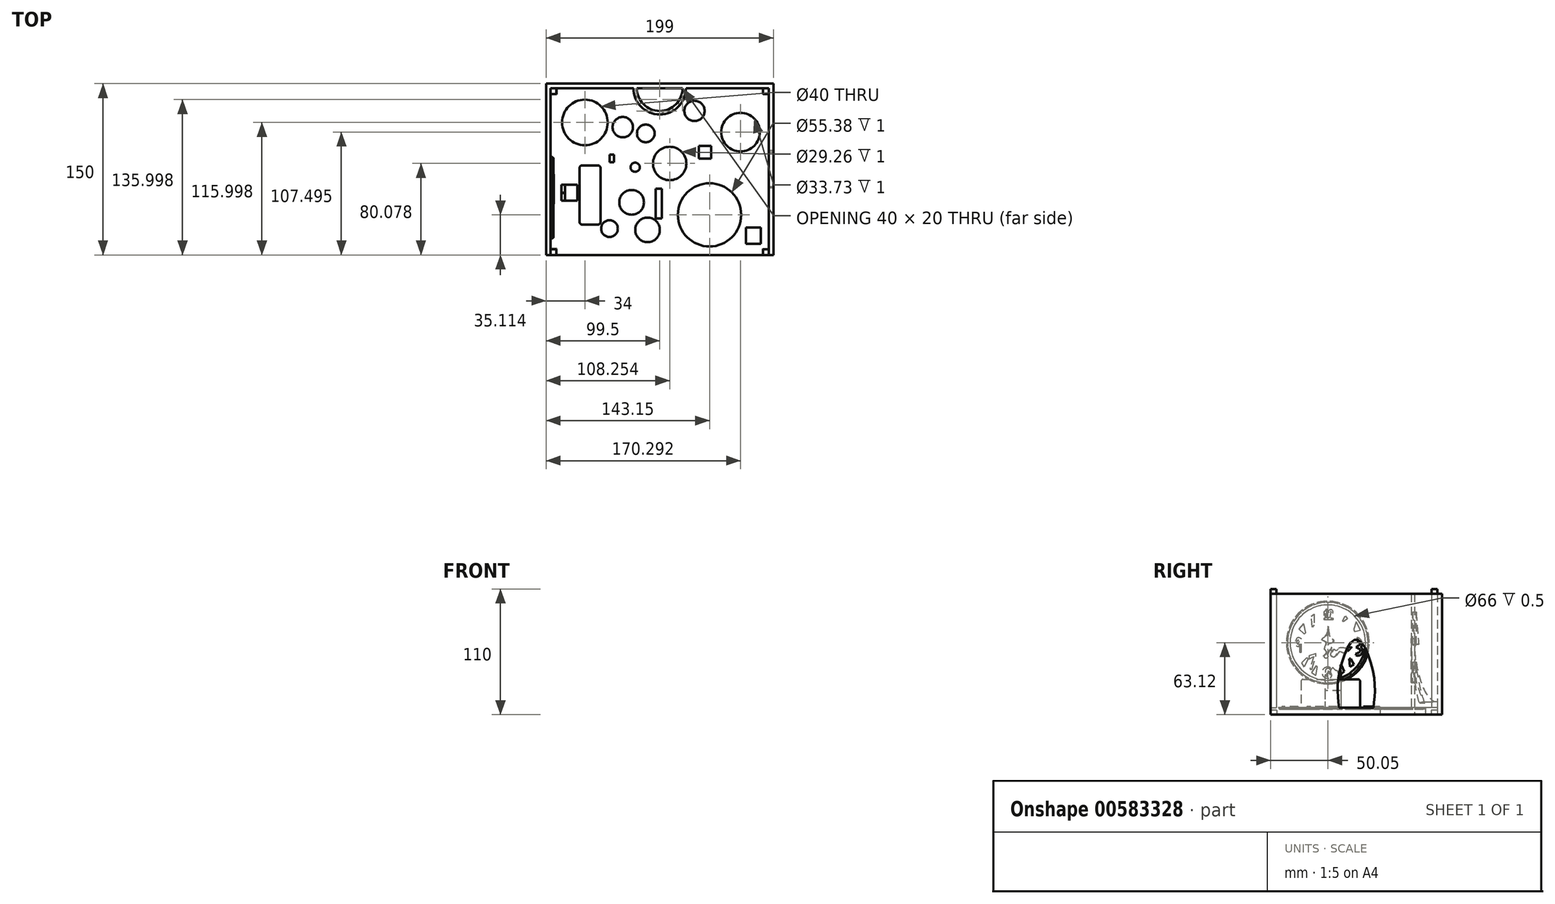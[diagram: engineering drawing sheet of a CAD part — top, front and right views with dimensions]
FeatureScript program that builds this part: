
annotation { "Feature Type Name" : "Feature", "Feature Type Description" : "" }
export const myFeature = defineFeature(function(context is Context, id is Id, definition is map)
    precondition{}
    {
        {
            var Q0;
            Q0=qCreatedBy(makeId("Top.planeOp"),FACE);
            var sketch = newSketch(context, id + "F0", { "sketchPlane" : qUnion([Q0])});
            skLineSegment(sketch, "E0.bottom", {"start": v(-124.6, 78.2) * mm, "end": v(74.4, 78.2) * mm});
            skLineSegment(sketch, "E0.top", {"start": v(-124.6, -71.8) * mm, "end": v(74.4, -71.8) * mm});
            skLineSegment(sketch, "E0.left", {"start": v(-124.6, 78.2) * mm, "end": v(-124.6, -71.8) * mm});
            skLineSegment(sketch, "E0.right", {"start": v(74.4, 78.2) * mm, "end": v(74.4, -71.8) * mm});
            skLineSegment(sketch, "E1.0", {"start": v(-120.6, 74.2) * mm, "end": v(-120.6, -71.8) * mm});
            skLineSegment(sketch, "E1.1", {"start": v(-120.6, 74.2) * mm, "end": v(70.4, 74.2) * mm});
            skLineSegment(sketch, "E1.2", {"start": v(70.4, 74.2) * mm, "end": v(70.4, -71.8) * mm});
            skSolve(sketch);
        }
        {
            var Q0;
            Q0 = qSketchRegion(id + "F0", true);
            extrude(context, id + "F1", {"entities" : qUnion([Q0]), "depth" : 6 * mm, "offsetDistance" : 25 * mm});
        }
        {
            var Q0;
            Q0=makeQuery(id+"F1.opExtrude","CAP_FACE",FACE,{"disambiguationData":[OSD([sQuery(id+"F0.wireOp",EDGE,"E0.bottom"),sQuery(id+"F0.wireOp",EDGE,"E0.top"),sQuery(id+"F0.wireOp",EDGE,"E0.left"),sQuery(id+"F0.wireOp",EDGE,"E0.right")])],"isStart":false});
            var sketch = newSketch(context, id + "F2", { "sketchPlane" : qUnion([Q0])});
            skLineSegment(sketch, "E2.0", {"start": v(-120.6, 74.2) * mm, "end": v(-120.6, -71.8) * mm});
            skLineSegment(sketch, "E2.1", {"start": v(-120.6, 74.2) * mm, "end": v(70.4, 74.2) * mm});
            skLineSegment(sketch, "E2.2", {"start": v(70.4, 74.2) * mm, "end": v(70.4, -71.8) * mm});
            skLineSegment(sketch, "E3", {"start": v(-120.6, -71.8) * mm, "end": v(-124.6, -71.8) * mm});
            skLineSegment(sketch, "E4", {"start": v(-124.6, -71.8) * mm, "end": v(-124.6, 78.2) * mm});
            skLineSegment(sketch, "E5", {"start": v(-124.6, 78.2) * mm, "end": v(74.4, 78.2) * mm});
            skLineSegment(sketch, "E6", {"start": v(74.4, 78.2) * mm, "end": v(74.4, -71.8) * mm});
            skLineSegment(sketch, "E7", {"start": v(74.4, -71.8) * mm, "end": v(70.4, -71.8) * mm});
            skPoint(sketch, "E8.start.orphan", {"position": v(-25.1, 64.2) * mm});
            skArc(sketch, "E9", {"start": v(-45.1, 74.2) * mm, "mid": v(-25.1, 54.2) * mm, "end": v(-5.1, 74.2) * mm});
            skArc(sketch, "E10.0", {"start": v(-48.1, 74.2) * mm, "mid": v(-25.1, 51.2) * mm, "end": v(-2.1, 74.2) * mm});
            skSolve(sketch);
        }
        {
            var Q0;
            Q0 = qSketchRegion(id + "F2", true);
            extrude(context, id + "F3", {"entities" : qUnion([Q0]), "operationType" : NewBodyOperationType.ADD, "depth" : 100 * mm, "offsetDistance" : 25 * mm});
        }
        {
            var Q0;
            Q0=makeQuery(id+"F3.boolean.opBoolean","MERGE",FACE,{"derivedFrom":[makeQuery(id+"F1.opExtrude","SWEPT_FACE",FACE,{"disambiguationData":[OSD([sQuery(id+"F0.wireOp",EDGE,"E0.right")])]}),makeQuery(id+"F3.opExtrude","SWEPT_FACE",FACE,{"disambiguationData":[OSD([sQuery(id+"F2.wireOp",EDGE,"E6")])]})]});
            var sketch = newSketch(context, id + "F4", { "sketchPlane" : qUnion([Q0])});
            skLineSegment(sketch, "E11", {"start": v(3.2, 6) * mm, "end": v(-11.8, 6) * mm});
            skLineSegment(sketch, "E12", {"start": v(3.2, 6) * mm, "end": v(18.2, 6) * mm});
            skPoint(sketch, "E13.start.orphan", {"position": v(3.2, 0) * mm});
            skPoint(sketch, "E14.1.internal.snap0", {"position": v(3.2, 36) * mm});
            skPoint(sketch, "E14.3.internal.snap0", {"position": v(3.2, 36) * mm});
            skFitSpline(sketch, "E14", {"points": [v(-11.8, 6) * mm, v(-11.8, 36) * mm, v(3.2, 66) * mm, v(18.2, 36) * mm, v(18.2, 6) * mm], "startDerivative": vector(-14.19, 109.03) * mm, "endDerivative": vector(-14.19, -109.03) * mm});
            skSolve(sketch);
        }
        {
            var Q0;
            Q0 = qSketchRegion(id + "F4", true);
            extrude(context, id + "F5", {"entities" : qUnion([Q0]), "operationType" : NewBodyOperationType.REMOVE, "oppositeDirection" : true, "depth" : 4 * mm, "offsetDistance" : 25 * mm});
        }
        {
            var Q0;
            Q0=makeQuery(id+"F1.opExtrude","CAP_FACE",FACE,{"disambiguationData":[OSD([sQuery(id+"F0.wireOp",EDGE,"E0.bottom"),sQuery(id+"F0.wireOp",EDGE,"E0.top"),sQuery(id+"F0.wireOp",EDGE,"E0.left"),sQuery(id+"F0.wireOp",EDGE,"E0.right")])],"isStart":true});
            var sketch = newSketch(context, id + "F6", { "sketchPlane" : qUnion([Q0])});
            skLineSegment(sketch, "E15.0", {"start": v(-120.6, -74.2) * mm, "end": v(-120.6, 71.8) * mm});
            skLineSegment(sketch, "E15.1", {"start": v(-120.6, -74.2) * mm, "end": v(70.4, -74.2) * mm});
            skLineSegment(sketch, "E15.2", {"start": v(70.4, -74.2) * mm, "end": v(70.4, 71.8) * mm});
            skLineSegment(sketch, "E16.bottom", {"start": v(-120.6, -74.2) * mm, "end": v(-115.1, -74.2) * mm});
            skLineSegment(sketch, "E16.top", {"start": v(-120.6, -68.7) * mm, "end": v(-115.1, -68.7) * mm});
            skLineSegment(sketch, "E16.left", {"start": v(-120.6, -74.2) * mm, "end": v(-120.6, -68.7) * mm});
            skLineSegment(sketch, "E16.right", {"start": v(-115.1, -74.2) * mm, "end": v(-115.1, -68.7) * mm});
            skLineSegment(sketch, "E17", {"start": v(70.4, 71.8) * mm, "end": v(64.9, 71.8) * mm});
            skLineSegment(sketch, "E18", {"start": v(64.9, 71.8) * mm, "end": v(64.9, 66.3) * mm});
            skLineSegment(sketch, "E19", {"start": v(64.9, 66.3) * mm, "end": v(70.4, 66.3) * mm});
            skLineSegment(sketch, "E20", {"start": v(70.4, 66.3) * mm, "end": v(70.4, 71.8) * mm});
            skLineSegment(sketch, "E21", {"start": v(-120.6, 71.8) * mm, "end": v(-115.1, 71.8) * mm});
            skLineSegment(sketch, "E22", {"start": v(-115.1, 71.8) * mm, "end": v(-115.1, 66.3) * mm});
            skLineSegment(sketch, "E23", {"start": v(-115.1, 66.3) * mm, "end": v(-120.6, 66.3) * mm});
            skLineSegment(sketch, "E24", {"start": v(-120.6, 66.3) * mm, "end": v(-120.6, 71.8) * mm});
            skLineSegment(sketch, "E25.bottom", {"start": v(70.4, -74.2) * mm, "end": v(64.9, -74.2) * mm});
            skLineSegment(sketch, "E25.top", {"start": v(70.4, -68.7) * mm, "end": v(64.9, -68.7) * mm});
            skLineSegment(sketch, "E25.left", {"start": v(70.4, -74.2) * mm, "end": v(70.4, -68.7) * mm});
            skLineSegment(sketch, "E25.right", {"start": v(64.9, -74.2) * mm, "end": v(64.9, -68.7) * mm});
            skSolve(sketch);
        }
        {
            var Q0;
            Q0 = qSketchRegion(id + "F6", true);
            extrude(context, id + "F7", {"entities" : qUnion([Q0]), "operationType" : NewBodyOperationType.REMOVE, "oppositeDirection" : true, "depth" : 4 * mm, "offsetDistance" : 25 * mm});
        }
        {
            var Q0;
            {var subQ4=sQuery(id+"F0.wireOp",EDGE,"E0.top");Q0=makeQuery(id+"F5.boolean.opBoolean","MERGE",FACE,{"derivedFrom":[makeQuery(id+"F3.boolean.opBoolean","SPLIT",FACE,{"disambiguationData":[TD([makeQuery(id+"F1.opExtrude","SWEPT_FACE",FACE,{"disambiguationData":[OSD([subQ4])]})])],"derivedFrom":makeQuery(id+"F1.opExtrude","CAP_FACE",FACE,{"disambiguationData":[OSD([sQuery(id+"F0.wireOp",EDGE,"E0.bottom"),subQ4,sQuery(id+"F0.wireOp",EDGE,"E0.left"),sQuery(id+"F0.wireOp",EDGE,"E0.right")])],"isStart":false})}),makeQuery(id+"F5.opExtrude","SWEPT_FACE",FACE,{"disambiguationData":[OSD([sQuery(id+"F4.wireOp",EDGE,"E11"),sQuery(id+"F4.wireOp",EDGE,"E12")])]})]});}
            var sketch = newSketch(context, id + "F8", { "sketchPlane" : qUnion([Q0])});
            skLineSegment(sketch, "E26.bottom", {"start": v(-120.6, 74.2) * mm, "end": v(-115.6, 74.2) * mm});
            skLineSegment(sketch, "E26.top", {"start": v(-120.6, 69.2) * mm, "end": v(-115.6, 69.2) * mm});
            skLineSegment(sketch, "E26.left", {"start": v(-120.6, 74.2) * mm, "end": v(-120.6, 69.2) * mm});
            skLineSegment(sketch, "E26.right", {"start": v(-115.6, 74.2) * mm, "end": v(-115.6, 69.2) * mm});
            skLineSegment(sketch, "E27.bottom", {"start": v(-120.6, -71.8) * mm, "end": v(-115.6, -71.8) * mm});
            skLineSegment(sketch, "E27.top", {"start": v(-120.6, -66.8) * mm, "end": v(-115.6, -66.8) * mm});
            skLineSegment(sketch, "E27.left", {"start": v(-120.6, -71.8) * mm, "end": v(-120.6, -66.8) * mm});
            skLineSegment(sketch, "E27.right", {"start": v(-115.6, -71.8) * mm, "end": v(-115.6, -66.8) * mm});
            skLineSegment(sketch, "E28.bottom", {"start": v(70.4, -71.8) * mm, "end": v(65.4, -71.8) * mm});
            skLineSegment(sketch, "E28.top", {"start": v(70.4, -66.8) * mm, "end": v(65.4, -66.8) * mm});
            skLineSegment(sketch, "E28.left", {"start": v(70.4, -71.8) * mm, "end": v(70.4, -66.8) * mm});
            skLineSegment(sketch, "E28.right", {"start": v(65.4, -71.8) * mm, "end": v(65.4, -66.8) * mm});
            skLineSegment(sketch, "E29.bottom", {"start": v(70.4, 74.2) * mm, "end": v(65.4, 74.2) * mm});
            skLineSegment(sketch, "E29.top", {"start": v(70.4, 69.2) * mm, "end": v(65.4, 69.2) * mm});
            skLineSegment(sketch, "E29.left", {"start": v(70.4, 74.2) * mm, "end": v(70.4, 69.2) * mm});
            skLineSegment(sketch, "E29.right", {"start": v(65.4, 74.2) * mm, "end": v(65.4, 69.2) * mm});
            skSolve(sketch);
        }
        {
            var Q0;
            Q0 = qSketchRegion(id + "F8", true);
            extrude(context, id + "F9", {"entities" : qUnion([Q0]), "operationType" : NewBodyOperationType.ADD, "depth" : 104 * mm, "offsetDistance" : 25 * mm});
        }
        {
            var Q0;
            {var subQ4=sQuery(id+"F0.wireOp",EDGE,"E0.top");Q0=makeQuery(id+"F5.boolean.opBoolean","MERGE",FACE,{"derivedFrom":[makeQuery(id+"F3.boolean.opBoolean","SPLIT",FACE,{"disambiguationData":[TD([makeQuery(id+"F1.opExtrude","SWEPT_FACE",FACE,{"disambiguationData":[OSD([subQ4])]})])],"derivedFrom":makeQuery(id+"F1.opExtrude","CAP_FACE",FACE,{"disambiguationData":[OSD([sQuery(id+"F0.wireOp",EDGE,"E0.bottom"),subQ4,sQuery(id+"F0.wireOp",EDGE,"E0.left"),sQuery(id+"F0.wireOp",EDGE,"E0.right")])],"isStart":false})}),makeQuery(id+"F5.opExtrude","SWEPT_FACE",FACE,{"disambiguationData":[OSD([sQuery(id+"F4.wireOp",EDGE,"E11"),sQuery(id+"F4.wireOp",EDGE,"E12")])]})]});}
            var sketch = newSketch(context, id + "F10", { "sketchPlane" : qUnion([Q0])});
            skCircle(sketch, "E30", {"center": v(-90.6, 44.2) * mm, "radius": 20 * mm});
            skSolve(sketch);
        }
        {
            var Q0;
            Q0 = qSketchRegion(id + "F10", true);
            extrude(context, id + "F11", {"entities" : qUnion([Q0]), "operationType" : NewBodyOperationType.REMOVE, "oppositeDirection" : true, "depth" : 25 * mm, "offsetDistance" : 25 * mm});
        }
        {
            var Q0;
            {var subQ0=sQuery(id+"F2.wireOp",EDGE,"E9");Q0=makeQuery(id+"F3.boolean.opBoolean","SPLIT",FACE,{"disambiguationData":[TD([makeQuery(id+"F3.opExtrude","SWEPT_FACE",FACE,{"disambiguationData":[OSD([subQ0])]})])],"derivedFrom":makeQuery(id+"F1.opExtrude","CAP_FACE",FACE,{"disambiguationData":[OSD([sQuery(id+"F0.wireOp",EDGE,"E0.bottom"),sQuery(id+"F0.wireOp",EDGE,"E0.top"),sQuery(id+"F0.wireOp",EDGE,"E0.left"),sQuery(id+"F0.wireOp",EDGE,"E0.right")])],"isStart":false})});}
            var sketch = newSketch(context, id + "F12", { "sketchPlane" : qUnion([Q0])});
            skSolve(sketch);
        }
        {
            var Q0;
            {var subQ0=sQuery(id+"F2.wireOp",EDGE,"E9");Q0=makeQuery(id+"F12.imprint","IMPRINT",FACE,{"disambiguationData":[TD([[makeQuery(id+"F12.imprint","IMPRINT",EDGE,{"derivedFrom":makeQuery(id+"F3.opExtrude","CAP_EDGE",EDGE,{"disambiguationData":[OSD([subQ0])],"isStart":true})}),1.0]])]});}
            extrude(context, id + "F13", {"entities" : qUnion([Q0]), "operationType" : NewBodyOperationType.REMOVE, "oppositeDirection" : true, "depth" : 25 * mm, "offsetDistance" : 25 * mm});
        }
        {
            var Q0;
            {var subQ4=sQuery(id+"F0.wireOp",EDGE,"E0.top");Q0=makeQuery(id+"F5.boolean.opBoolean","MERGE",FACE,{"derivedFrom":[makeQuery(id+"F3.boolean.opBoolean","SPLIT",FACE,{"disambiguationData":[TD([makeQuery(id+"F1.opExtrude","SWEPT_FACE",FACE,{"disambiguationData":[OSD([subQ4])]})])],"derivedFrom":makeQuery(id+"F1.opExtrude","CAP_FACE",FACE,{"disambiguationData":[OSD([sQuery(id+"F0.wireOp",EDGE,"E0.bottom"),subQ4,sQuery(id+"F0.wireOp",EDGE,"E0.left"),sQuery(id+"F0.wireOp",EDGE,"E0.right")])],"isStart":false})}),makeQuery(id+"F5.opExtrude","SWEPT_FACE",FACE,{"disambiguationData":[OSD([sQuery(id+"F4.wireOp",EDGE,"E11"),sQuery(id+"F4.wireOp",EDGE,"E12")])]})]});}
            var sketch = newSketch(context, id + "F14", { "sketchPlane" : qUnion([Q0])});
            skLineSegment(sketch, "E31.bottom", {"start": v(-95.22, -45.16) * mm, "end": v(-77.03, -45.16) * mm});
            skLineSegment(sketch, "E31.top", {"start": v(-95.22, 6.58) * mm, "end": v(-77.03, 6.58) * mm});
            skLineSegment(sketch, "E31.left", {"start": v(-95.22, -45.16) * mm, "end": v(-95.22, 6.58) * mm});
            skLineSegment(sketch, "E31.right", {"start": v(-77.03, -45.16) * mm, "end": v(-77.03, 6.58) * mm});
            skSolve(sketch);
        }
        {
            var Q0;
            Q0 = qSketchRegion(id + "F14", true);
            extrude(context, id + "F15", {"entities" : qUnion([Q0]), "operationType" : NewBodyOperationType.ADD, "depth" : 25 * mm, "offsetDistance" : 25 * mm});
        }
        {
            var Q0;
            {var subQ4=sQuery(id+"F0.wireOp",EDGE,"E0.top");Q0=makeQuery(id+"F5.boolean.opBoolean","MERGE",FACE,{"derivedFrom":[makeQuery(id+"F3.boolean.opBoolean","SPLIT",FACE,{"disambiguationData":[TD([makeQuery(id+"F1.opExtrude","SWEPT_FACE",FACE,{"disambiguationData":[OSD([subQ4])]})])],"derivedFrom":makeQuery(id+"F1.opExtrude","CAP_FACE",FACE,{"disambiguationData":[OSD([sQuery(id+"F0.wireOp",EDGE,"E0.bottom"),subQ4,sQuery(id+"F0.wireOp",EDGE,"E0.left"),sQuery(id+"F0.wireOp",EDGE,"E0.right")])],"isStart":false})}),makeQuery(id+"F5.opExtrude","SWEPT_FACE",FACE,{"disambiguationData":[OSD([sQuery(id+"F4.wireOp",EDGE,"E11"),sQuery(id+"F4.wireOp",EDGE,"E12")])]})]});}
            var sketch = newSketch(context, id + "F16", { "sketchPlane" : qUnion([Q0])});
            skLineSegment(sketch, "E32.bottom", {"start": v(-111.18, -10.16) * mm, "end": v(-97.18, -10.16) * mm});
            skLineSegment(sketch, "E32.top", {"start": v(-111.18, -24.16) * mm, "end": v(-97.18, -24.16) * mm});
            skLineSegment(sketch, "E32.left", {"start": v(-111.18, -10.16) * mm, "end": v(-111.18, -24.16) * mm});
            skLineSegment(sketch, "E32.right", {"start": v(-97.18, -10.16) * mm, "end": v(-97.18, -24.16) * mm});
            skSolve(sketch);
        }
        {
            var Q0;
            Q0 = qSketchRegion(id + "F16", true);
            extrude(context, id + "F17", {"entities" : qUnion([Q0]), "operationType" : NewBodyOperationType.ADD, "depth" : 15 * mm, "offsetDistance" : 25 * mm});
        }
        {
            var Q0;
            Q0=makeQuery(id+"F17.opExtrude","CAP_FACE",FACE,{"disambiguationData":[OSD([sQuery(id+"F16.wireOp",EDGE,"E32.bottom"),sQuery(id+"F16.wireOp",EDGE,"E32.top"),sQuery(id+"F16.wireOp",EDGE,"E32.left"),sQuery(id+"F16.wireOp",EDGE,"E32.right")])],"isStart":false});
            var sketch = newSketch(context, id + "F18", { "sketchPlane" : qUnion([Q0])});
            skLineSegment(sketch, "E33.bottom", {"start": v(-111.18, -10.16) * mm, "end": v(-108.12, -10.16) * mm});
            skLineSegment(sketch, "E33.top", {"start": v(-111.18, -24.16) * mm, "end": v(-108.12, -24.16) * mm});
            skLineSegment(sketch, "E33.left", {"start": v(-111.18, -10.16) * mm, "end": v(-111.18, -24.16) * mm});
            skLineSegment(sketch, "E33.right", {"start": v(-108.12, -10.16) * mm, "end": v(-108.12, -24.16) * mm});
            skSolve(sketch);
        }
        {
            var Q0;
            Q0 = qSketchRegion(id + "F18", true);
            extrude(context, id + "F19", {"entities" : qUnion([Q0]), "operationType" : NewBodyOperationType.ADD, "depth" : 20 * mm, "offsetDistance" : 25 * mm});
        }
        {
            var Q0;
            Q0=makeQuery(id+"F19.boolean.opBoolean","MERGE",FACE,{"derivedFrom":[makeQuery(id+"F17.opExtrude","SWEPT_FACE",FACE,{"disambiguationData":[OSD([sQuery(id+"F16.wireOp",EDGE,"E32.left")])]}),makeQuery(id+"F19.opExtrude","SWEPT_FACE",FACE,{"disambiguationData":[OSD([sQuery(id+"F18.wireOp",EDGE,"E33.left")])]})]});
            var sketch = newSketch(context, id + "F20", { "sketchPlane" : qUnion([Q0])});
            skFitSpline(sketch, "E34", {"points": [v(10.16, 36.34) * mm, v(12.41, 36.34) * mm, v(12.96, 37.99) * mm, v(15.43, 39.09) * mm, v(17.16, 41) * mm, v(19, 39.36) * mm, v(19.83, 36.9) * mm, v(22.02, 38.54) * mm, v(24.16, 34.42) * mm, v(24.16, 35.24) * mm], "startDerivative": vector(26.42, -5.74) * mm, "endDerivative": vector(-1.87, 21.7) * mm});
            skLineSegment(sketch, "E35", {"start": v(10.16, 36.34) * mm, "end": v(10.16, 41) * mm});
            skLineSegment(sketch, "E36", {"start": v(10.16, 41) * mm, "end": v(24.16, 41) * mm});
            skLineSegment(sketch, "E37", {"start": v(24.16, 41) * mm, "end": v(24.2, 34.77) * mm});
            skSolve(sketch);
        }
        {
            var Q0;
            Q0 = qSketchRegion(id + "F20", true);
            var Q1;
            {var subQ0=sQuery(id+"F20.wireOp",EDGE,"E36");var subQ1=sQuery(id+"F20.wireOp",EDGE,"E34");var subQ2=makeQuery(id+"F20.imprint","INTERSECT",VERTEX,{"disambiguationData":[OD(1.0)],"derivedFrom":[subQ1,subQ0]});Q1=makeQuery(id+"F20.imprint","IMPRINT",FACE,{"disambiguationData":[TD([[makeQuery(id+"F20.imprint","IMPRINT",EDGE,{"disambiguationData":[TD([[subQ2,-1.0]])],"derivedFrom":subQ1}),1.0]])]});}
            extrude(context, id + "F21", {"entities" : qUnion([Q0, Q1]), "operationType" : NewBodyOperationType.REMOVE, "oppositeDirection" : true, "depth" : 25 * mm, "offsetDistance" : 25 * mm});
        }
        {
            var Q0;
            Q0=makeQuery(id+"F15.opExtrude","CAP_FACE",FACE,{"disambiguationData":[OSD([sQuery(id+"F14.wireOp",EDGE,"E31.bottom"),sQuery(id+"F14.wireOp",EDGE,"E31.top"),sQuery(id+"F14.wireOp",EDGE,"E31.left"),sQuery(id+"F14.wireOp",EDGE,"E31.right")])],"isStart":false});
            var Q1;
            Q1=makeQuery(id+"F15.opExtrude","SWEPT_EDGE",EDGE,{"disambiguationData":[OSD([sQuery(id+"F14.wireOp",EDGE,"E31.top"),sQuery(id+"F14.wireOp",EDGE,"E31.right")])]});
            var Q2;
            Q2=makeQuery(id+"F15.opExtrude","SWEPT_EDGE",EDGE,{"disambiguationData":[OSD([sQuery(id+"F14.wireOp",EDGE,"E31.top"),sQuery(id+"F14.wireOp",EDGE,"E31.left")])]});
            var Q3;
            Q3=makeQuery(id+"F15.opExtrude","SWEPT_EDGE",EDGE,{"disambiguationData":[OSD([sQuery(id+"F14.wireOp",EDGE,"E31.bottom"),sQuery(id+"F14.wireOp",EDGE,"E31.left")])]});
            var Q4;
            Q4=makeQuery(id+"F15.opExtrude","SWEPT_EDGE",EDGE,{"disambiguationData":[OSD([sQuery(id+"F14.wireOp",EDGE,"E31.bottom"),sQuery(id+"F14.wireOp",EDGE,"E31.right")])]});
            fillet(context, id + "F22", {"entities" : qUnion([Q0, Q1, Q2, Q3, Q4]), "radius" : 2 * mm, "tangentPropagation" : true, "allowEdgeOverflow" : false});
        }
        {
            var Q0;
            Q0=makeQuery(id+"F3.opExtrude","SWEPT_FACE",FACE,{"disambiguationData":[OSD([sQuery(id+"F2.wireOp",EDGE,"E2.0")])]});
            var sketch = newSketch(context, id + "F23", { "sketchPlane" : qUnion([Q0])});
            skCircle(sketch, "E38", {"center": v(-21.75, 63.12) * mm, "radius": 36.22 * mm});
            skSolve(sketch);
        }
        {
            var Q0;
            Q0 = qSketchRegion(id + "F23", true);
            extrude(context, id + "F24", {"entities" : qUnion([Q0]), "operationType" : NewBodyOperationType.ADD, "depth" : 1 * mm, "offsetDistance" : 25 * mm});
        }
        {
            var Q0;
            Q0=makeQuery(id+"F24.opExtrude","CAP_FACE",FACE,{"disambiguationData":[OSD([sQuery(id+"F23.wireOp",EDGE,"E38")])],"isStart":false});
            var sketch = newSketch(context, id + "F25", { "sketchPlane" : qUnion([Q0])});
            skCircle(sketch, "E39.0", {"center": v(-21.75, 63.12) * mm, "radius": 35.22 * mm});
            skCircle(sketch, "E40.0", {"center": v(-21.75, 63.12) * mm, "radius": 41.22 * mm});
            skSolve(sketch);
        }
        {
            var Q0;
            Q0=makeQuery(id+"F25.imprint","IMPRINT",FACE,{"disambiguationData":[TD([[makeQuery(id+"F25.imprint","IMPRINT",EDGE,{"derivedFrom":sQuery(id+"F25.wireOp",EDGE,"E39.0")}),1.0]])]});
            extrude(context, id + "F26", {"entities" : qUnion([Q0]), "operationType" : NewBodyOperationType.ADD, "depth" : .8 * mm, "offsetDistance" : 25 * mm});
        }
        {
            var Q0;
            Q0=makeQuery(id+"F26.opExtrude","CAP_FACE",FACE,{"disambiguationData":[OSD([sQuery(id+"F25.wireOp",EDGE,"E39.0")])],"isStart":false});
            var sketch = newSketch(context, id + "F27", { "sketchPlane" : qUnion([Q0])});
            skCircle(sketch, "E41", {"center": v(-21.75, 63.12) * mm, "radius": 33 * mm});
            skCircle(sketch, "E42", {"center": v(-21.75, 63.12) * mm, "radius": 35.22 * mm});
            skPoint(sketch, "E42.first.point", {"position": v(-50.69, 83.2) * mm});
            skPoint(sketch, "E42.second.point", {"position": v(6.83, 42.54) * mm});
            skPoint(sketch, "E42.third.point", {"position": v(-37.98, 31.86) * mm});
            skSolve(sketch);
        }
        {
            var Q0;
            Q0 = qSketchRegion(id + "F27", true);
            extrude(context, id + "F28", {"entities" : qUnion([Q0]), "operationType" : NewBodyOperationType.ADD, "depth" : .5 * mm, "offsetDistance" : 25 * mm});
        }
        {
            var Q0;
            Q0=makeQuery(id+"F24.opExtrude","CAP_EDGE",EDGE,{"disambiguationData":[OSD([sQuery(id+"F23.wireOp",EDGE,"E38")])],"isStart":false});
            var Q1;
            Q1=makeQuery(id+"F28.opExtrude","CAP_EDGE",EDGE,{"disambiguationData":[OSD([sQuery(id+"F27.wireOp",EDGE,"E42")])],"isStart":false});
            fillet(context, id + "F29", {"entities" : qUnion([Q0, Q1]), "radius" : .5 * mm, "tangentPropagation" : true, "allowEdgeOverflow" : false});
        }
        {
            var Q0;
            Q0=makeQuery(id+"F26.opExtrude","CAP_FACE",FACE,{"disambiguationData":[OSD([sQuery(id+"F25.wireOp",EDGE,"E39.0")])],"isStart":false});
            var sketch = newSketch(context, id + "F30", { "sketchPlane" : qUnion([Q0])});
            skLineSegment(sketch, "E43", {"start": v(-21.75, 83.12) * mm, "end": v(-24.75, 83.12) * mm});
            skLineSegment(sketch, "E44", {"start": v(-24.75, 83.12) * mm, "end": v(-24.75, 84.62) * mm});
            skLineSegment(sketch, "E45", {"start": v(-24.75, 84.62) * mm, "end": v(-23.75, 84.62) * mm});
            skLineSegment(sketch, "E46", {"start": v(-23.75, 84.62) * mm, "end": v(-23.75, 88.82) * mm});
            skLineSegment(sketch, "E47", {"start": v(-23.75, 88.82) * mm, "end": v(-24.75, 86.72) * mm});
            skPoint(sketch, "E47.endSnap0", {"position": v(-23.75, 86.72) * mm});
            skLineSegment(sketch, "E48", {"start": v(-24.75, 86.72) * mm, "end": v(-24.75, 90.21) * mm});
            skLineSegment(sketch, "E49", {"start": v(-21.75, 83.12) * mm, "end": v(-21.75, 84.62) * mm});
            skLineSegment(sketch, "E50", {"start": v(-21.75, 84.62) * mm, "end": v(-22.75, 84.62) * mm});
            skLineSegment(sketch, "E51", {"start": v(-22.75, 84.62) * mm, "end": v(-22.75, 90.21) * mm});
            skLineSegment(sketch, "E52", {"start": v(-22.75, 90.21) * mm, "end": v(-22.75, 92.71) * mm});
            skLineSegment(sketch, "E53", {"start": v(-22.75, 92.71) * mm, "end": v(-24.75, 90.21) * mm});
            skLineSegment(sketch, "E54", {"start": v(-21.49, 90.33) * mm, "end": v(-20.48, 89.37) * mm});
            skFitSpline(sketch, "E55", {"points": [v(-21.75, 84.62) * mm, v(-19.91, 85.71) * mm, v(-19.13, 88.42) * mm, v(-19.01, 90.33) * mm, v(-19.69, 90.33) * mm, v(-20.48, 89.37) * mm], "startDerivative": vector(9.35, 3.5) * mm, "endDerivative": vector(-4.01, -6.7) * mm});
            skFitSpline(sketch, "E56", {"points": [v(-21.49, 90.33) * mm, v(-19.91, 92.08) * mm, v(-18.23, 91.92) * mm, v(-17.55, 89.37) * mm, v(-18.57, 85.71) * mm, v(-19.24, 84.62) * mm], "startDerivative": vector(6.82, 10.65) * mm, "endDerivative": vector(-4.31, -5.89) * mm});
            skLineSegment(sketch, "E57", {"start": v(-19.24, 84.62) * mm, "end": v(-17.33, 84.62) * mm});
            skLineSegment(sketch, "E58", {"start": v(-17.33, 84.62) * mm, "end": v(-17.33, 82.85) * mm});
            skLineSegment(sketch, "E59", {"start": v(-17.33, 82.85) * mm, "end": v(-21.75, 83.12) * mm});
            skLineSegment(sketch, "E60", {"start": v(-8.82, 82.38) * mm, "end": v(-6.44, 86.59) * mm});
            skLineSegment(sketch, "E61", {"start": v(-6.44, 86.59) * mm, "end": v(-4.45, 84.06) * mm});
            skLineSegment(sketch, "E62", {"start": v(-4.45, 84.06) * mm, "end": v(-7.92, 81.34) * mm});
            skLineSegment(sketch, "E63", {"start": v(-7.92, 81.34) * mm, "end": v(-8.82, 82.38) * mm});
            skLineSegment(sketch, "E64", {"start": v(0.9, 74.52) * mm, "end": v(1.7, 72.84) * mm});
            skLineSegment(sketch, "E65", {"start": v(1.7, 72.84) * mm, "end": v(6.85, 73.96) * mm});
            skLineSegment(sketch, "E66", {"start": v(6.85, 73.96) * mm, "end": v(3.08, 81.34) * mm});
            skLineSegment(sketch, "E67", {"start": v(3.08, 81.34) * mm, "end": v(0.9, 74.52) * mm});
            skLineSegment(sketch, "E68", {"start": v(3.68, 67.5) * mm, "end": v(3.68, 64.42) * mm});
            skArc(sketch, "E69", {"start": v(3.68, 60.21) * mm, "mid": v(6.26, 62.32) * mm, "end": v(3.68, 64.42) * mm});
            skArc(sketch, "E70", {"start": v(3.68, 54.32) * mm, "mid": v(6.52, 56.14) * mm, "end": v(3.68, 57.97) * mm});
            skLineSegment(sketch, "E71", {"start": v(3.68, 57.97) * mm, "end": v(3.68, 60.21) * mm});
            skLineSegment(sketch, "E72", {"start": v(3.68, 54.32) * mm, "end": v(2.9, 52) * mm});
            skArc(sketch, "E73", {"start": v(2.9, 52) * mm, "mid": v(8.12, 53.68) * mm, "end": v(7.25, 59.1) * mm});
            skPoint(sketch, "E73.endSnap0", {"position": v(3.68, 59.1) * mm});
            skArc(sketch, "E74", {"start": v(7.25, 59.1) * mm, "mid": v(7.92, 64.34) * mm, "end": v(3.68, 67.5) * mm});
            skLineSegment(sketch, "E75", {"start": v(-1.68, 48.99) * mm, "end": v(1.1, 43.94) * mm});
            skLineSegment(sketch, "E76", {"start": v(1.1, 43.94) * mm, "end": v(-2.17, 42.14) * mm});
            skLineSegment(sketch, "E77", {"start": v(-2.17, 42.14) * mm, "end": v(-3.07, 48.99) * mm});
            skLineSegment(sketch, "E78", {"start": v(-3.07, 48.99) * mm, "end": v(-1.48, 48.99) * mm});
            skLineSegment(sketch, "E79", {"start": v(-11.4, 43.38) * mm, "end": v(-10.2, 35.24) * mm});
            skLineSegment(sketch, "E80", {"start": v(-10.2, 35.24) * mm, "end": v(-7.43, 37.77) * mm});
            skLineSegment(sketch, "E81", {"start": v(-7.43, 37.77) * mm, "end": v(-10, 43.66) * mm});
            skLineSegment(sketch, "E82", {"start": v(-10, 43.66) * mm, "end": v(-11.4, 43.38) * mm});
            skArc(sketch, "E83", {"start": v(-19.53, 41.13) * mm, "mid": v(-26.78, 36.62) * mm, "end": v(-19.33, 32.44) * mm});
            skArc(sketch, "E84", {"start": v(-19.33, 32.44) * mm, "mid": v(-19.17, 36.77) * mm, "end": v(-23.5, 36.73) * mm});
            skArc(sketch, "E85", {"start": v(-19.53, 39.17) * mm, "mid": v(-22.84, 40.1) * mm, "end": v(-23.5, 36.73) * mm});
            skLineSegment(sketch, "E86", {"start": v(-19.53, 39.17) * mm, "end": v(-19.53, 41.13) * mm});
            skCircle(sketch, "E87", {"center": v(-21.32, 34.68) * mm, "radius": 1.78 * mm});
            skPoint(sketch, "E88.start.orphan", {"position": v(-21.75, 63.12) * mm});
            skLineSegment(sketch, "E89", {"start": v(-32.23, 42.82) * mm, "end": v(-36, 36.92) * mm});
            skLineSegment(sketch, "E90", {"start": v(-36, 36.92) * mm, "end": v(-32.01, 34.37) * mm});
            skLineSegment(sketch, "E91", {"start": v(-32.01, 34.37) * mm, "end": v(-31.04, 41.7) * mm});
            skLineSegment(sketch, "E92", {"start": v(-31.04, 41.7) * mm, "end": v(-32.23, 42.82) * mm});
            skLineSegment(sketch, "E93", {"start": v(-40.17, 49.83) * mm, "end": v(-39.17, 48.7) * mm});
            skLineSegment(sketch, "E94", {"start": v(-39.17, 48.7) * mm, "end": v(-42.35, 41.7) * mm});
            skLineSegment(sketch, "E95", {"start": v(-42.35, 41.7) * mm, "end": v(-44.53, 45.62) * mm});
            skLineSegment(sketch, "E96", {"start": v(-44.53, 45.62) * mm, "end": v(-40.17, 49.83) * mm});
            skFitSpline(sketch, "E97", {"points": [v(-44.93, 66.39) * mm, v(-47.9, 67.5) * mm, v(-49.89, 64.98) * mm, v(-49.69, 60.77) * mm, v(-47.11, 59.93) * mm, v(-46.52, 61.9) * mm, v(-46.52, 62.18) * mm], "startDerivative": vector(-16.37, 10.26) * mm, "endDerivative": vector(-0.08, 3.23) * mm});
            skLineSegment(sketch, "E98", {"start": v(-46.52, 62.18) * mm, "end": v(-46.52, 54.6) * mm});
            skLineSegment(sketch, "E99", {"start": v(-46.52, 54.6) * mm, "end": v(-44.93, 54.6) * mm});
            skLineSegment(sketch, "E100", {"start": v(-44.93, 54.6) * mm, "end": v(-44.93, 66.39) * mm});
            skFitSpline(sketch, "E101", {"points": [v(-47.11, 64.98) * mm, v(-48.7, 64.42) * mm, v(-48.5, 62.12) * mm, v(-47.53, 62.18) * mm, v(-47.11, 64.98) * mm]});
            skLineSegment(sketch, "E102", {"start": v(-46.99, 74.94) * mm, "end": v(-42.37, 70.7) * mm});
            skLineSegment(sketch, "E103", {"start": v(-42.37, 70.7) * mm, "end": v(-41.2, 71.98) * mm});
            skLineSegment(sketch, "E104", {"start": v(-41.2, 71.98) * mm, "end": v(-42.83, 79.83) * mm});
            skLineSegment(sketch, "E105", {"start": v(-42.83, 79.83) * mm, "end": v(-46.99, 74.94) * mm});
            skLineSegment(sketch, "E106", {"start": v(-36.37, 86.04) * mm, "end": v(-33.6, 88) * mm});
            skLineSegment(sketch, "E107", {"start": v(-33.6, 88) * mm, "end": v(-33.6, 78.53) * mm});
            skLineSegment(sketch, "E108", {"start": v(-33.6, 78.53) * mm, "end": v(-35.21, 76.57) * mm});
            skLineSegment(sketch, "E109", {"start": v(-35.21, 76.57) * mm, "end": v(-36.37, 86.04) * mm});
            skLineSegment(sketch, "E110", {"start": v(-38.13, 51.55) * mm, "end": v(-38.13, 48.7) * mm});
            skLineSegment(sketch, "E111", {"start": v(-38.13, 48.7) * mm, "end": v(-33.92, 50.89) * mm});
            skLineSegment(sketch, "E112", {"start": v(-33.92, 50.89) * mm, "end": v(-37.2, 41.13) * mm});
            skLineSegment(sketch, "E113", {"start": v(-37.2, 41.13) * mm, "end": v(-37.2, 39.8) * mm});
            skLineSegment(sketch, "E114", {"start": v(-37.2, 39.8) * mm, "end": v(-35.56, 39.8) * mm});
            skLineSegment(sketch, "E115", {"start": v(-35.56, 39.8) * mm, "end": v(-32.17, 51.22) * mm});
            skLineSegment(sketch, "E116", {"start": v(-32.17, 51.22) * mm, "end": v(-32.17, 53.37) * mm});
            skLineSegment(sketch, "E117", {"start": v(-32.17, 53.37) * mm, "end": v(-38.13, 51.55) * mm});
            skSolve(sketch);
        }
        {
            var Q0;
            Q0 = qSketchRegion(id + "F30", true);
            extrude(context, id + "F31", {"entities" : qUnion([Q0]), "operationType" : NewBodyOperationType.REMOVE, "oppositeDirection" : true, "depth" : 1 * mm, "offsetDistance" : 25 * mm});
        }
        {
            var Q0;
            Q0=makeQuery(id+"F31.boolean.opBoolean","SPLIT",FACE,{"disambiguationData":[TD([makeQuery(id+"F28.opExtrude","SWEPT_FACE",FACE,{"disambiguationData":[OSD([sQuery(id+"F27.wireOp",EDGE,"E41")])]})])],"derivedFrom":makeQuery(id+"F26.opExtrude","CAP_FACE",FACE,{"disambiguationData":[OSD([sQuery(id+"F25.wireOp",EDGE,"E39.0")])],"isStart":false})});
            var sketch = newSketch(context, id + "F32", { "sketchPlane" : qUnion([Q0])});
            skFitSpline(sketch, "E118", {"points": [v(-21.24, 77.22) * mm, v(-23.48, 69.5) * mm, v(-26.98, 65.55) * mm, v(-23.34, 63.18) * mm, v(-25.02, 58.43) * mm, v(-23.03, 54.4) * mm, v(-25.33, 51.51) * mm, v(-25.33, 51.15) * mm], "startDerivative": vector(-3.35, -41.55) * mm, "endDerivative": vector(3.56, -6.91) * mm});
            skFitSpline(sketch, "E119", {"points": [v(-21.24, 77.22) * mm, v(-19.62, 68.85) * mm, v(-16.64, 63.8) * mm, v(-21.24, 61.27) * mm, v(-18.43, 58.46) * mm, v(-21.24, 54.8) * mm, v(-21.24, 51.51) * mm], "startDerivative": vector(0.02, -40.88) * mm, "endDerivative": vector(7.92, -24.89) * mm});
            skArc(sketch, "E120", {"start": v(-25.33, 51.15) * mm, "mid": v(-23.14, 49.66) * mm, "end": v(-21.24, 51.51) * mm});
            skSolve(sketch);
        }
        {
            var Q0;
            Q0 = qSketchRegion(id + "F32", true);
            extrude(context, id + "F33", {"entities" : qUnion([Q0]), "operationType" : NewBodyOperationType.ADD, "depth" : 1 * mm, "offsetDistance" : 25 * mm});
        }
        {
            var Q0;
            Q0=makeQuery(id+"F33.opExtrude","CAP_FACE",FACE,{"disambiguationData":[OSD([sQuery(id+"F32.wireOp",EDGE,"E118"),sQuery(id+"F32.wireOp",EDGE,"E119"),sQuery(id+"F32.wireOp",EDGE,"E120")])],"isStart":false});
            fillet(context, id + "F34", {"entities" : qUnion([Q0]), "radius" : .3 * mm, "tangentPropagation" : true, "allowEdgeOverflow" : false});
        }
        {
            var Q0;
            Q0=makeQuery(id+"F31.boolean.opBoolean","SPLIT",FACE,{"disambiguationData":[TD([makeQuery(id+"F28.opExtrude","SWEPT_FACE",FACE,{"disambiguationData":[OSD([sQuery(id+"F27.wireOp",EDGE,"E41")])]})])],"derivedFrom":makeQuery(id+"F26.opExtrude","CAP_FACE",FACE,{"disambiguationData":[OSD([sQuery(id+"F25.wireOp",EDGE,"E39.0")])],"isStart":false})});
            var sketch = newSketch(context, id + "F35", { "sketchPlane" : qUnion([Q0])});
            skFitSpline(sketch, "E121", {"points": [v(-19.12, 52.06) * mm, v(-16.17, 57.27) * mm, v(-14.45, 56.23) * mm, v(-11.75, 58.66) * mm, v(-3.4, 58.31) * mm, v(-0.94, 59) * mm, v(-7.33, 54.14) * mm, v(-11.5, 55.18) * mm, v(-15.68, 50.67) * mm, v(-19.12, 52.06) * mm]});
            skSolve(sketch);
        }
        {
            var Q0;
            Q0 = qSketchRegion(id + "F35", true);
            extrude(context, id + "F36", {"entities" : qUnion([Q0]), "operationType" : NewBodyOperationType.ADD, "depth" : 1 * mm, "offsetDistance" : 25 * mm});
        }
        {
            var Q0;
            Q0=makeQuery(id+"F36.opExtrude","CAP_FACE",FACE,{"disambiguationData":[OSD([sQuery(id+"F35.wireOp",EDGE,"E121")])],"isStart":false});
            fillet(context, id + "F37", {"entities" : qUnion([Q0]), "radius" : .3 * mm, "tangentPropagation" : true, "allowEdgeOverflow" : false});
        }
        {
            var Q0;
            {var subQ4=sQuery(id+"F0.wireOp",EDGE,"E0.top");Q0=makeQuery(id+"F5.boolean.opBoolean","MERGE",FACE,{"derivedFrom":[makeQuery(id+"F3.boolean.opBoolean","SPLIT",FACE,{"disambiguationData":[TD([makeQuery(id+"F1.opExtrude","SWEPT_FACE",FACE,{"disambiguationData":[OSD([subQ4])]})])],"derivedFrom":makeQuery(id+"F1.opExtrude","CAP_FACE",FACE,{"disambiguationData":[OSD([sQuery(id+"F0.wireOp",EDGE,"E0.bottom"),subQ4,sQuery(id+"F0.wireOp",EDGE,"E0.left"),sQuery(id+"F0.wireOp",EDGE,"E0.right")])],"isStart":false})}),makeQuery(id+"F5.opExtrude","SWEPT_FACE",FACE,{"disambiguationData":[OSD([sQuery(id+"F4.wireOp",EDGE,"E11"),sQuery(id+"F4.wireOp",EDGE,"E12")])]})]});}
            var sketch = newSketch(context, id + "F38", { "sketchPlane" : qUnion([Q0])});
            skCircle(sketch, "E122", {"center": v(-46.6, 4.99) * mm, "radius": 4.03 * mm});
            skCircle(sketch, "E123", {"center": v(18.54, -36.69) * mm, "radius": 27.69 * mm});
            skCircle(sketch, "E124", {"center": v(5.36, 54.34) * mm, "radius": 8.88 * mm});
            skCircle(sketch, "E125", {"center": v(-69.09, -48.75) * mm, "radius": 7.32 * mm});
            skCircle(sketch, "E126", {"center": v(-49.7, -25.72) * mm, "radius": 10.8 * mm});
            skCircle(sketch, "E127", {"center": v(45.68, 35.7) * mm, "radius": 16.87 * mm});
            skCircle(sketch, "E128", {"center": v(-16.36, 8.28) * mm, "radius": 14.63 * mm});
            skCircle(sketch, "E129", {"center": v(-57.46, 40.08) * mm, "radius": 8.9 * mm});
            skCircle(sketch, "E130", {"center": v(-37.3, 34.6) * mm, "radius": 7.72 * mm});
            skCircle(sketch, "E131", {"center": v(-35.74, -49.85) * mm, "radius": 10.75 * mm});
            skSolve(sketch);
        }
        {
            var Q0;
            Q0 = qSketchRegion(id + "F38", true);
            extrude(context, id + "F39", {"entities" : qUnion([Q0]), "operationType" : NewBodyOperationType.REMOVE, "oppositeDirection" : true, "depth" : 1 * mm, "offsetDistance" : 25 * mm});
        }
        {
            var Q0;
            {var subQ4=sQuery(id+"F0.wireOp",EDGE,"E0.top");Q0=makeQuery(id+"F5.boolean.opBoolean","MERGE",FACE,{"derivedFrom":[makeQuery(id+"F3.boolean.opBoolean","SPLIT",FACE,{"disambiguationData":[TD([makeQuery(id+"F1.opExtrude","SWEPT_FACE",FACE,{"disambiguationData":[OSD([subQ4])]})])],"derivedFrom":makeQuery(id+"F1.opExtrude","CAP_FACE",FACE,{"disambiguationData":[OSD([sQuery(id+"F0.wireOp",EDGE,"E0.bottom"),subQ4,sQuery(id+"F0.wireOp",EDGE,"E0.left"),sQuery(id+"F0.wireOp",EDGE,"E0.right")])],"isStart":false})}),makeQuery(id+"F5.opExtrude","SWEPT_FACE",FACE,{"disambiguationData":[OSD([sQuery(id+"F4.wireOp",EDGE,"E11"),sQuery(id+"F4.wireOp",EDGE,"E12")])]})]});}
            var sketch = newSketch(context, id + "F40", { "sketchPlane" : qUnion([Q0])});
            skLineSegment(sketch, "E132.bottom", {"start": v(-69.09, 15.95) * mm, "end": v(-65.21, 15.95) * mm});
            skLineSegment(sketch, "E132.top", {"start": v(-69.09, 9.37) * mm, "end": v(-65.21, 9.37) * mm});
            skLineSegment(sketch, "E132.left", {"start": v(-69.09, 15.95) * mm, "end": v(-69.09, 9.37) * mm});
            skLineSegment(sketch, "E132.right", {"start": v(-65.21, 15.95) * mm, "end": v(-65.21, 9.37) * mm});
            skLineSegment(sketch, "E133.bottom", {"start": v(-28.76, -13.66) * mm, "end": v(-23.34, -13.66) * mm});
            skLineSegment(sketch, "E133.top", {"start": v(-28.76, -39.98) * mm, "end": v(-23.34, -39.98) * mm});
            skLineSegment(sketch, "E133.left", {"start": v(-28.76, -13.66) * mm, "end": v(-28.76, -39.98) * mm});
            skLineSegment(sketch, "E133.right", {"start": v(-23.34, -13.66) * mm, "end": v(-23.34, -39.98) * mm});
            skLineSegment(sketch, "E134.bottom", {"start": v(9.23, 23.63) * mm, "end": v(20.1, 23.63) * mm});
            skLineSegment(sketch, "E134.top", {"start": v(9.23, 12.66) * mm, "end": v(20.1, 12.66) * mm});
            skLineSegment(sketch, "E134.left", {"start": v(9.23, 23.63) * mm, "end": v(9.23, 12.66) * mm});
            skLineSegment(sketch, "E134.right", {"start": v(20.1, 23.63) * mm, "end": v(20.1, 12.66) * mm});
            skLineSegment(sketch, "E135.bottom", {"start": v(50.33, -47.65) * mm, "end": v(63.52, -47.65) * mm});
            skLineSegment(sketch, "E135.top", {"start": v(50.33, -61.91) * mm, "end": v(63.52, -61.91) * mm});
            skLineSegment(sketch, "E135.left", {"start": v(50.33, -47.65) * mm, "end": v(50.33, -61.91) * mm});
            skLineSegment(sketch, "E135.right", {"start": v(63.52, -47.65) * mm, "end": v(63.52, -61.91) * mm});
            skSolve(sketch);
        }
        {
            var Q0;
            Q0 = qSketchRegion(id + "F40", true);
            extrude(context, id + "F41", {"entities" : qUnion([Q0]), "operationType" : NewBodyOperationType.ADD, "depth" : 1 * mm, "offsetDistance" : 25 * mm});
        }
        {
            var Q0;
            {var subQ0=sQuery(id+"F2.wireOp",EDGE,"E2.1");var subQ1=sQuery(id+"F2.wireOp",EDGE,"E9");Q0=makeQuery(id+"F13.boolean.opBoolean","MERGE",FACE,{"derivedFrom":[makeQuery(id+"F3.opExtrude","SWEPT_FACE",FACE,{"disambiguationData":[OSD([subQ0]),TDD([makeQuery(id+"F2.imprint","IMPRINT",EDGE,{"disambiguationData":[TD([[makeQuery(id+"F2.imprint","INTERSECT",VERTEX,{"disambiguationData":[OD(0.0)],"derivedFrom":[subQ0,subQ1]}),-1.0]])],"derivedFrom":subQ0})])]}),makeQuery(id+"F13.opExtrude","SWEPT_FACE",FACE,{"disambiguationData":[OSD([subQ0])]})]});}
            var sketch = newSketch(context, id + "F42", { "sketchPlane" : qUnion([Q0])});
            skLineSegment(sketch, "E136", {"start": v(-17.58, 89.95) * mm, "end": v(-13.44, 61.8) * mm});
            skLineSegment(sketch, "E137", {"start": v(-13.44, 61.8) * mm, "end": v(-17.5, 61.21) * mm});
            skLineSegment(sketch, "E138", {"start": v(-17.5, 61.21) * mm, "end": v(-17.58, 89.95) * mm});
            skLineSegment(sketch, "E139", {"start": v(-22.54, 66.77) * mm, "end": v(-17.58, 28.7) * mm});
            skLineSegment(sketch, "E140", {"start": v(-17.58, 28.7) * mm, "end": v(-21.65, 28.18) * mm});
            skLineSegment(sketch, "E141", {"start": v(-21.65, 28.18) * mm, "end": v(-22.54, 66.77) * mm});
            skLineSegment(sketch, "E142", {"start": v(-17.58, 46.09) * mm, "end": v(-5.1, 11.33) * mm});
            skLineSegment(sketch, "E143", {"start": v(-5.1, 11.33) * mm, "end": v(-8.3, 10.19) * mm});
            skLineSegment(sketch, "E144", {"start": v(-8.3, 10.19) * mm, "end": v(-17.58, 46.09) * mm});
            skSolve(sketch);
        }
        {
            var Q0;
            Q0 = qSketchRegion(id + "F42", true);
            extrude(context, id + "F43", {"entities" : qUnion([Q0]), "operationType" : NewBodyOperationType.REMOVE, "depth" : 49 * mm, "offsetDistance" : 25 * mm});
        }
    });
